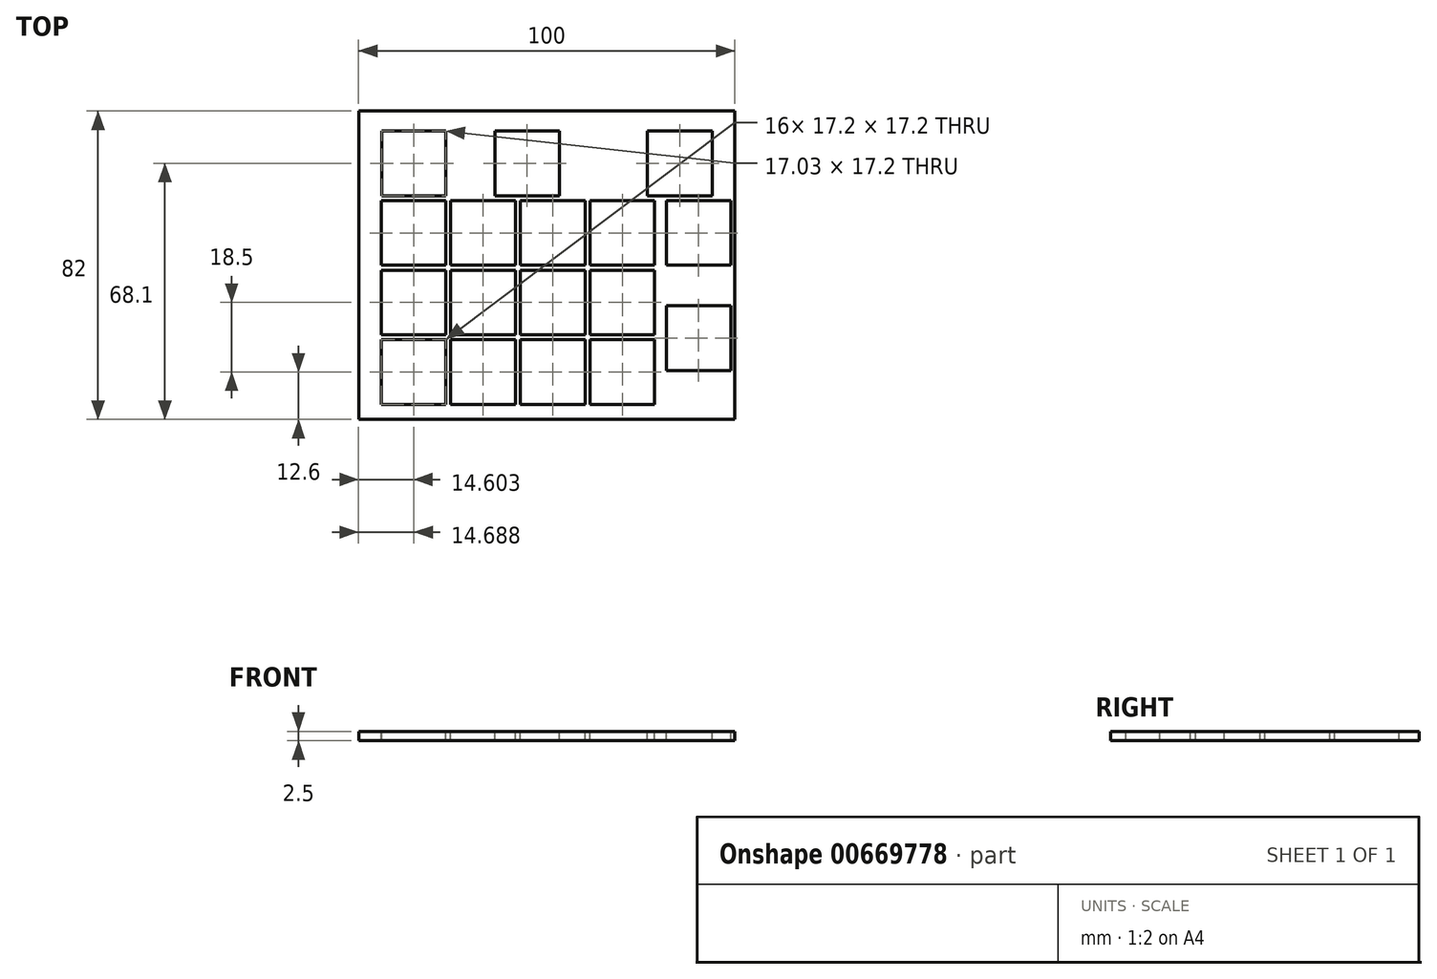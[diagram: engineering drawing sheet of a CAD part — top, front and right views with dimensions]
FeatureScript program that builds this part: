
annotation { "Feature Type Name" : "Feature", "Feature Type Description" : "" }
export const myFeature = defineFeature(function(context is Context, id is Id, definition is map)
    precondition{}
    {
        {
            var Q0;
            Q0=qCreatedBy(makeId("Top.planeOp"),FACE);
            var sketch = newSketch(context, id + "F0", { "sketchPlane" : qUnion([Q0])});
            skLineSegment(sketch, "E0.bottom", {"start": v(-89.14, 0) * mm, "end": v(10.86, 0) * mm});
            skLineSegment(sketch, "E0.top", {"start": v(-89.14, -82) * mm, "end": v(10.86, -82) * mm});
            skLineSegment(sketch, "E0.left", {"start": v(-89.14, 0) * mm, "end": v(-89.14, -82) * mm});
            skLineSegment(sketch, "E0.right", {"start": v(10.86, 0) * mm, "end": v(10.86, -82) * mm});
            skSolve(sketch);
        }
        {
            var Q0;
            Q0=makeQuery(id+"F0.imprint","IMPRINT",FACE,{"disambiguationData":[TD([[makeQuery(id+"F0.imprint","IMPRINT",EDGE,{"derivedFrom":sQuery(id+"F0.wireOp",EDGE,"E0.bottom")}),-1.0]])]});
            extrude(context, id + "F1", {"entities" : qUnion([Q0]), "depth" : 2.5 * mm, "offsetDistance" : 25 * mm});
        }
        {
            var Q0;
            Q0=makeQuery(id+"F1.opExtrude","CAP_FACE",FACE,{"disambiguationData":[OSD([sQuery(id+"F0.wireOp",EDGE,"E0.bottom"),sQuery(id+"F0.wireOp",EDGE,"E0.top"),sQuery(id+"F0.wireOp",EDGE,"E0.left"),sQuery(id+"F0.wireOp",EDGE,"E0.right")])],"isStart":false});
            var sketch = newSketch(context, id + "F2", { "sketchPlane" : qUnion([Q0])});
            skLineSegment(sketch, "E1.bottom", {"start": v(-83.14, -78) * mm, "end": v(-65.94, -78) * mm});
            skLineSegment(sketch, "E1.top", {"start": v(-83.14, -60.8) * mm, "end": v(-65.94, -60.8) * mm});
            skLineSegment(sketch, "E1.left", {"start": v(-83.14, -78) * mm, "end": v(-83.14, -60.8) * mm});
            skLineSegment(sketch, "E1.right", {"start": v(-65.94, -78) * mm, "end": v(-65.94, -60.8) * mm});
            skLineSegment(sketch, "E2.bottom", {"start": v(-65.94, -59.5) * mm, "end": v(-83.14, -59.5) * mm});
            skLineSegment(sketch, "E2.top", {"start": v(-65.94, -42.3) * mm, "end": v(-83.14, -42.3) * mm});
            skLineSegment(sketch, "E2.left", {"start": v(-65.94, -59.5) * mm, "end": v(-65.94, -42.3) * mm});
            skLineSegment(sketch, "E2.right", {"start": v(-83.14, -59.5) * mm, "end": v(-83.14, -42.3) * mm});
            skLineSegment(sketch, "E3.bottom", {"start": v(-65.94, -41) * mm, "end": v(-83.14, -41) * mm});
            skLineSegment(sketch, "E3.top", {"start": v(-65.94, -23.8) * mm, "end": v(-83.14, -23.8) * mm});
            skLineSegment(sketch, "E3.left", {"start": v(-65.94, -41) * mm, "end": v(-65.94, -23.8) * mm});
            skLineSegment(sketch, "E3.right", {"start": v(-83.14, -41) * mm, "end": v(-83.14, -23.8) * mm});
            skLineSegment(sketch, "E4.bottom", {"start": v(-65.94, -22.5) * mm, "end": v(-82.97, -22.5) * mm});
            skLineSegment(sketch, "E4.top", {"start": v(-65.94, -5.3) * mm, "end": v(-82.97, -5.3) * mm});
            skLineSegment(sketch, "E4.left", {"start": v(-65.94, -22.5) * mm, "end": v(-65.94, -5.3) * mm});
            skLineSegment(sketch, "E4.right", {"start": v(-82.97, -22.5) * mm, "end": v(-82.97, -5.3) * mm});
            skSolve(sketch);
        }
        {
            var Q0;
            Q0=makeQuery(id+"F2.imprint","IMPRINT",FACE,{"disambiguationData":[TD([[makeQuery(id+"F2.imprint","IMPRINT",EDGE,{"derivedFrom":sQuery(id+"F2.wireOp",EDGE,"E1.bottom")}),1.0]])]});
            extrude(context, id + "F3", {"entities" : qUnion([Q0]), "operationType" : NewBodyOperationType.REMOVE, "oppositeDirection" : true, "depth" : 25 * mm, "offsetDistance" : 25 * mm});
        }
        {
            var Q0;
            Q0 = qSketchRegion(id + "F2", true);
            extrude(context, id + "F4", {"entities" : qUnion([Q0]), "operationType" : NewBodyOperationType.REMOVE, "oppositeDirection" : true, "depth" : 25 * mm, "offsetDistance" : 25 * mm});
        }
        {
            var Q0;
            Q0=makeQuery(id+"F1.opExtrude","CAP_FACE",FACE,{"disambiguationData":[OSD([sQuery(id+"F0.wireOp",EDGE,"E0.bottom"),sQuery(id+"F0.wireOp",EDGE,"E0.top"),sQuery(id+"F0.wireOp",EDGE,"E0.left"),sQuery(id+"F0.wireOp",EDGE,"E0.right")])],"isStart":false});
            var sketch = newSketch(context, id + "F5", { "sketchPlane" : qUnion([Q0])});
            skLineSegment(sketch, "E5.bottom", {"start": v(-64.64, -78) * mm, "end": v(-47.44, -78) * mm});
            skLineSegment(sketch, "E5.top", {"start": v(-64.64, -60.8) * mm, "end": v(-47.44, -60.8) * mm});
            skLineSegment(sketch, "E5.left", {"start": v(-64.64, -78) * mm, "end": v(-64.64, -60.8) * mm});
            skLineSegment(sketch, "E5.right", {"start": v(-47.44, -78) * mm, "end": v(-47.44, -60.8) * mm});
            skLineSegment(sketch, "E6.bottom", {"start": v(-46.14, -78) * mm, "end": v(-28.94, -78) * mm});
            skLineSegment(sketch, "E6.top", {"start": v(-46.14, -60.8) * mm, "end": v(-28.94, -60.8) * mm});
            skLineSegment(sketch, "E6.left", {"start": v(-46.14, -78) * mm, "end": v(-46.14, -60.8) * mm});
            skLineSegment(sketch, "E6.right", {"start": v(-28.94, -78) * mm, "end": v(-28.94, -60.8) * mm});
            skLineSegment(sketch, "E7.bottom", {"start": v(-27.64, -78) * mm, "end": v(-10.44, -78) * mm});
            skLineSegment(sketch, "E7.top", {"start": v(-27.64, -60.8) * mm, "end": v(-10.44, -60.8) * mm});
            skLineSegment(sketch, "E7.left", {"start": v(-27.64, -78) * mm, "end": v(-27.64, -60.8) * mm});
            skLineSegment(sketch, "E7.right", {"start": v(-10.44, -78) * mm, "end": v(-10.44, -60.8) * mm});
            skSolve(sketch);
        }
        {
            var Q0;
            Q0 = qSketchRegion(id + "F5", true);
            extrude(context, id + "F6", {"entities" : qUnion([Q0]), "operationType" : NewBodyOperationType.REMOVE, "oppositeDirection" : true, "depth" : 25 * mm, "offsetDistance" : 25 * mm});
        }
        {
            var Q0;
            Q0=makeQuery(id+"F1.opExtrude","CAP_FACE",FACE,{"disambiguationData":[OSD([sQuery(id+"F0.wireOp",EDGE,"E0.bottom"),sQuery(id+"F0.wireOp",EDGE,"E0.top"),sQuery(id+"F0.wireOp",EDGE,"E0.left"),sQuery(id+"F0.wireOp",EDGE,"E0.right")])],"isStart":false});
            var sketch = newSketch(context, id + "F7", { "sketchPlane" : qUnion([Q0])});
            skLineSegment(sketch, "E8.bottom", {"start": v(-47.44, -59.5) * mm, "end": v(-64.64, -59.5) * mm});
            skLineSegment(sketch, "E8.top", {"start": v(-47.44, -42.3) * mm, "end": v(-64.64, -42.3) * mm});
            skLineSegment(sketch, "E8.left", {"start": v(-47.44, -59.5) * mm, "end": v(-47.44, -42.3) * mm});
            skLineSegment(sketch, "E8.right", {"start": v(-64.64, -59.5) * mm, "end": v(-64.64, -42.3) * mm});
            skLineSegment(sketch, "E9.bottom", {"start": v(-47.44, -41) * mm, "end": v(-64.64, -41) * mm});
            skLineSegment(sketch, "E9.top", {"start": v(-47.44, -23.8) * mm, "end": v(-64.64, -23.8) * mm});
            skLineSegment(sketch, "E9.left", {"start": v(-47.44, -41) * mm, "end": v(-47.44, -23.8) * mm});
            skLineSegment(sketch, "E9.right", {"start": v(-64.64, -41) * mm, "end": v(-64.64, -23.8) * mm});
            skPoint(sketch, "E10.firstSnap0", {"position": v(-47.44, -32.4) * mm});
            skLineSegment(sketch, "E11.bottom", {"start": v(-28.94, -59.5) * mm, "end": v(-46.14, -59.5) * mm});
            skLineSegment(sketch, "E11.top", {"start": v(-28.94, -42.3) * mm, "end": v(-46.14, -42.3) * mm});
            skLineSegment(sketch, "E11.left", {"start": v(-28.94, -59.5) * mm, "end": v(-28.94, -42.3) * mm});
            skLineSegment(sketch, "E11.right", {"start": v(-46.14, -59.5) * mm, "end": v(-46.14, -42.3) * mm});
            skLineSegment(sketch, "E12.bottom", {"start": v(-28.94, -41) * mm, "end": v(-46.14, -41) * mm});
            skLineSegment(sketch, "E12.top", {"start": v(-28.94, -23.8) * mm, "end": v(-46.14, -23.8) * mm});
            skLineSegment(sketch, "E12.left", {"start": v(-28.94, -41) * mm, "end": v(-28.94, -23.8) * mm});
            skLineSegment(sketch, "E12.right", {"start": v(-46.14, -41) * mm, "end": v(-46.14, -23.8) * mm});
            skSolve(sketch);
        }
        {
            var Q0;
            Q0 = qSketchRegion(id + "F7", true);
            extrude(context, id + "F8", {"entities" : qUnion([Q0]), "operationType" : NewBodyOperationType.REMOVE, "oppositeDirection" : true, "depth" : 25 * mm, "offsetDistance" : 25 * mm});
        }
        {
            var Q0;
            Q0=makeQuery(id+"F1.opExtrude","CAP_FACE",FACE,{"disambiguationData":[OSD([sQuery(id+"F0.wireOp",EDGE,"E0.bottom"),sQuery(id+"F0.wireOp",EDGE,"E0.top"),sQuery(id+"F0.wireOp",EDGE,"E0.left"),sQuery(id+"F0.wireOp",EDGE,"E0.right")])],"isStart":false});
            var sketch = newSketch(context, id + "F9", { "sketchPlane" : qUnion([Q0])});
            skLineSegment(sketch, "E13.bottom", {"start": v(-27.64, -59.5) * mm, "end": v(-10.44, -59.5) * mm});
            skLineSegment(sketch, "E13.top", {"start": v(-27.64, -42.3) * mm, "end": v(-10.44, -42.3) * mm});
            skLineSegment(sketch, "E13.left", {"start": v(-27.64, -59.5) * mm, "end": v(-27.64, -42.3) * mm});
            skLineSegment(sketch, "E13.right", {"start": v(-10.44, -59.5) * mm, "end": v(-10.44, -42.3) * mm});
            skLineSegment(sketch, "E14.bottom", {"start": v(-27.64, -41) * mm, "end": v(-10.44, -41) * mm});
            skLineSegment(sketch, "E14.top", {"start": v(-27.64, -23.8) * mm, "end": v(-10.44, -23.8) * mm});
            skLineSegment(sketch, "E14.left", {"start": v(-27.64, -41) * mm, "end": v(-27.64, -23.8) * mm});
            skLineSegment(sketch, "E14.right", {"start": v(-10.44, -41) * mm, "end": v(-10.44, -23.8) * mm});
            skSolve(sketch);
        }
        {
            var Q0;
            Q0 = qSketchRegion(id + "F9", true);
            extrude(context, id + "F10", {"entities" : qUnion([Q0]), "operationType" : NewBodyOperationType.REMOVE, "oppositeDirection" : true, "depth" : 25 * mm, "offsetDistance" : 25 * mm});
        }
        {
            var Q0;
            Q0=makeQuery(id+"F1.opExtrude","CAP_FACE",FACE,{"disambiguationData":[OSD([sQuery(id+"F0.wireOp",EDGE,"E0.bottom"),sQuery(id+"F0.wireOp",EDGE,"E0.top"),sQuery(id+"F0.wireOp",EDGE,"E0.left"),sQuery(id+"F0.wireOp",EDGE,"E0.right")])],"isStart":false});
            var sketch = newSketch(context, id + "F11", { "sketchPlane" : qUnion([Q0])});
            skLineSegment(sketch, "E15.bottom", {"start": v(-7.34, -69) * mm, "end": v(9.86, -69) * mm});
            skLineSegment(sketch, "E15.top", {"start": v(-7.34, -51.8) * mm, "end": v(9.86, -51.8) * mm});
            skLineSegment(sketch, "E15.left", {"start": v(-7.34, -69) * mm, "end": v(-7.34, -51.8) * mm});
            skLineSegment(sketch, "E15.right", {"start": v(9.86, -69) * mm, "end": v(9.86, -51.8) * mm});
            skLineSegment(sketch, "E16.bottom", {"start": v(-7.34, -41) * mm, "end": v(9.86, -41) * mm});
            skLineSegment(sketch, "E16.top", {"start": v(-7.34, -23.8) * mm, "end": v(9.86, -23.8) * mm});
            skLineSegment(sketch, "E16.left", {"start": v(-7.34, -41) * mm, "end": v(-7.34, -23.8) * mm});
            skLineSegment(sketch, "E16.right", {"start": v(9.86, -41) * mm, "end": v(9.86, -23.8) * mm});
            skSolve(sketch);
        }
        {
            var Q0;
            Q0 = qSketchRegion(id + "F11", true);
            extrude(context, id + "F12", {"entities" : qUnion([Q0]), "operationType" : NewBodyOperationType.REMOVE, "oppositeDirection" : true, "depth" : 25 * mm, "offsetDistance" : 25 * mm});
        }
        {
            var Q0;
            Q0=makeQuery(id+"F1.opExtrude","CAP_FACE",FACE,{"disambiguationData":[OSD([sQuery(id+"F0.wireOp",EDGE,"E0.bottom"),sQuery(id+"F0.wireOp",EDGE,"E0.top"),sQuery(id+"F0.wireOp",EDGE,"E0.left"),sQuery(id+"F0.wireOp",EDGE,"E0.right")])],"isStart":false});
            var sketch = newSketch(context, id + "F13", { "sketchPlane" : qUnion([Q0])});
            skLineSegment(sketch, "E17.bottom", {"start": v(-52.94, -22.5) * mm, "end": v(-35.74, -22.5) * mm});
            skLineSegment(sketch, "E17.top", {"start": v(-52.94, -5.3) * mm, "end": v(-35.74, -5.3) * mm});
            skLineSegment(sketch, "E17.left", {"start": v(-52.94, -22.5) * mm, "end": v(-52.94, -5.3) * mm});
            skLineSegment(sketch, "E17.right", {"start": v(-35.74, -22.5) * mm, "end": v(-35.74, -5.3) * mm});
            skSolve(sketch);
        }
        {
            var Q0;
            Q0 = qSketchRegion(id + "F13", true);
            extrude(context, id + "F14", {"entities" : qUnion([Q0]), "operationType" : NewBodyOperationType.REMOVE, "oppositeDirection" : true, "depth" : 25 * mm, "offsetDistance" : 25 * mm});
        }
        {
            var Q0;
            Q0=makeQuery(id+"F1.opExtrude","CAP_FACE",FACE,{"disambiguationData":[OSD([sQuery(id+"F0.wireOp",EDGE,"E0.bottom"),sQuery(id+"F0.wireOp",EDGE,"E0.top"),sQuery(id+"F0.wireOp",EDGE,"E0.left"),sQuery(id+"F0.wireOp",EDGE,"E0.right")])],"isStart":false});
            var sketch = newSketch(context, id + "F15", { "sketchPlane" : qUnion([Q0])});
            skLineSegment(sketch, "E18.bottom", {"start": v(-12.34, -22.5) * mm, "end": v(4.86, -22.5) * mm});
            skLineSegment(sketch, "E18.top", {"start": v(-12.34, -5.3) * mm, "end": v(4.86, -5.3) * mm});
            skLineSegment(sketch, "E18.left", {"start": v(-12.34, -22.5) * mm, "end": v(-12.34, -5.3) * mm});
            skLineSegment(sketch, "E18.right", {"start": v(4.86, -22.5) * mm, "end": v(4.86, -5.3) * mm});
            skSolve(sketch);
        }
        {
            var Q0;
            Q0 = qSketchRegion(id + "F15", true);
            extrude(context, id + "F16", {"entities" : qUnion([Q0]), "operationType" : NewBodyOperationType.REMOVE, "oppositeDirection" : true, "depth" : 25 * mm, "offsetDistance" : 25 * mm});
        }
    });
